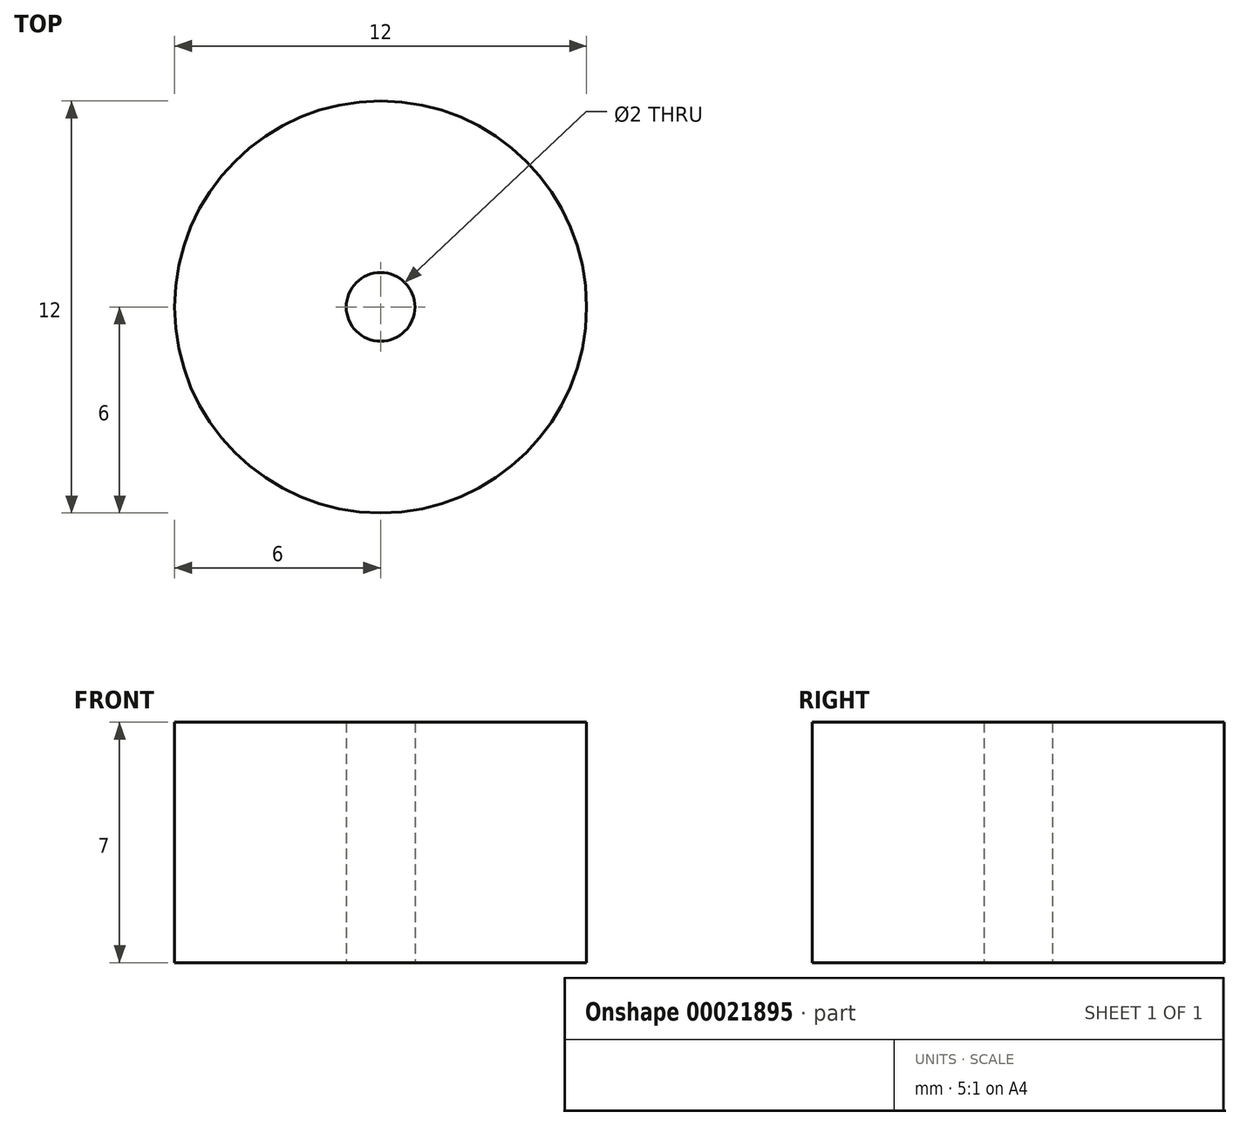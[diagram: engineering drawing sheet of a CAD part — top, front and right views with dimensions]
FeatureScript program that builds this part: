
annotation { "Feature Type Name" : "Feature", "Feature Type Description" : "" }
export const myFeature = defineFeature(function(context is Context, id is Id, definition is map)
    precondition{}
    {
        {
            var Q0;
            Q0=qCreatedBy(makeId("Top.planeOp"),FACE);
            var sketch = newSketch(context, id + "F0", { "sketchPlane" : qUnion([Q0])});
            skCircle(sketch, "E0", {"center": v(0, 0) * mm, "radius": 6 * mm});
            skCircle(sketch, "E1", {"center": v(0, 0) * mm, "radius": 1 * mm});
            skSolve(sketch);
        }
        {
            var Q0;
            Q0=makeQuery(id+"F0.imprint","IMPRINT",FACE,{"disambiguationData":[TD([[makeQuery(id+"F0.imprint","IMPRINT",EDGE,{"derivedFrom":sQuery(id+"F0.wireOp",EDGE,"E0")}),1.0]])]});
            extrude(context, id + "F1", {"entities" : qUnion([Q0]), "depth" : 7 * mm});
        }
    });
